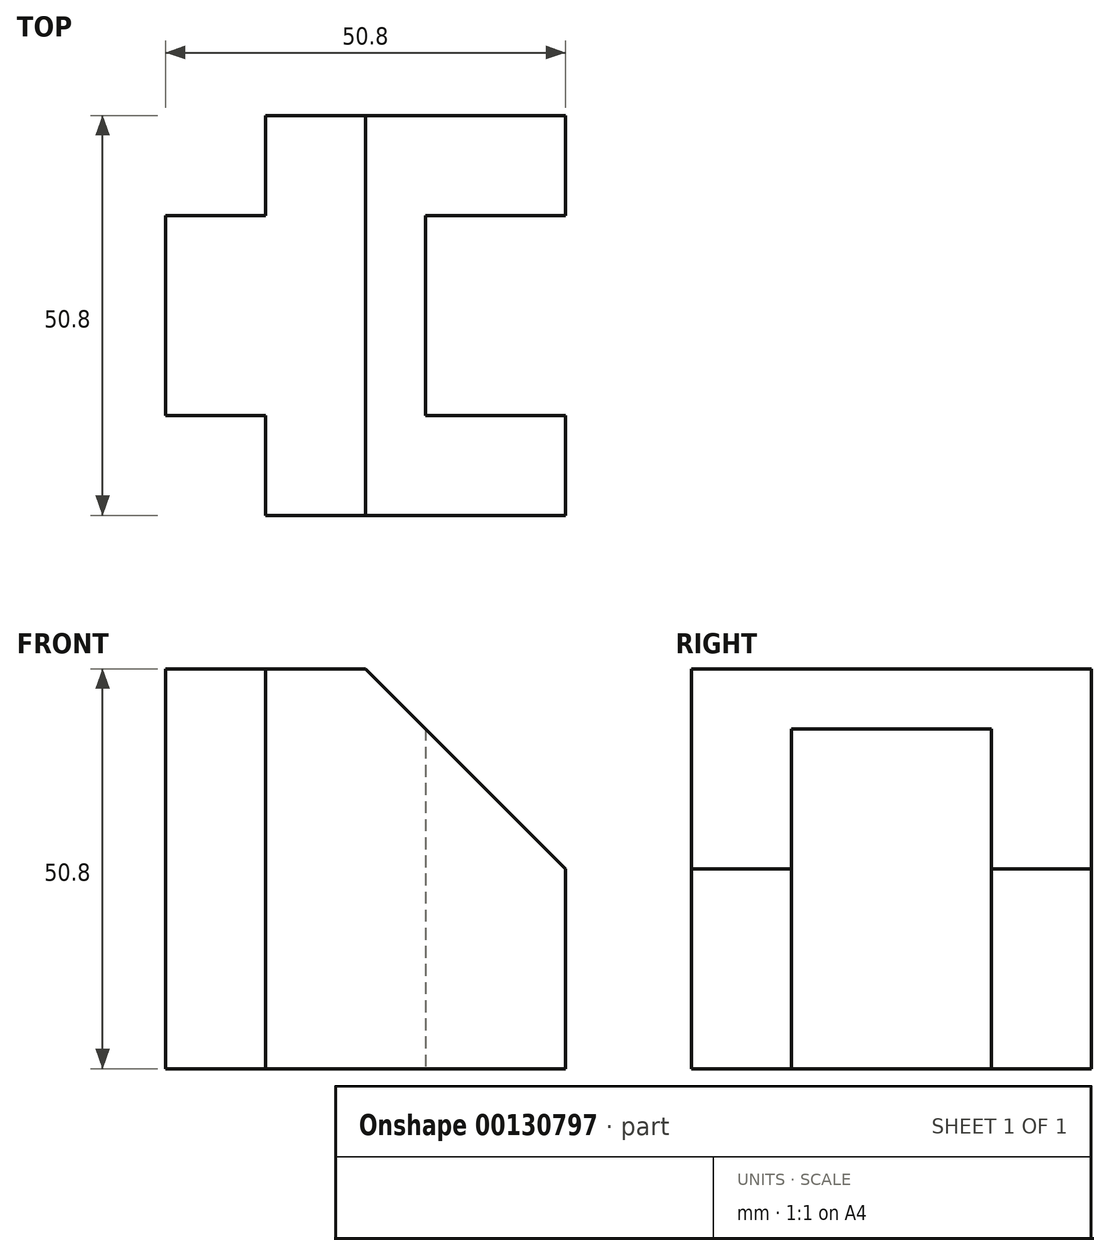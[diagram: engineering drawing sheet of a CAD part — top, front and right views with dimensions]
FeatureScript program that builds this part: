
annotation { "Feature Type Name" : "Feature", "Feature Type Description" : "" }
export const myFeature = defineFeature(function(context is Context, id is Id, definition is map)
    precondition{}
    {
        {
            var Q0;
            Q0=qCreatedBy(makeId("Top.planeOp"),FACE);
            var sketch = newSketch(context, id + "F0", { "sketchPlane" : qUnion([Q0])});
            skLineSegment(sketch, "E0", {"start": v(0, 0) * mm, "end": v(-12.7, 0) * mm});
            skLineSegment(sketch, "E1", {"start": v(-12.7, 0) * mm, "end": v(-12.7, -25.4) * mm});
            skLineSegment(sketch, "E2", {"start": v(-12.7, -25.4) * mm, "end": v(0, -25.4) * mm});
            skLineSegment(sketch, "E3", {"start": v(0, -25.4) * mm, "end": v(0, -38.1) * mm});
            skLineSegment(sketch, "E4", {"start": v(0, -38.1) * mm, "end": v(12.7, -38.1) * mm});
            skLineSegment(sketch, "E5", {"start": v(0, 0) * mm, "end": v(0, 12.7) * mm});
            skLineSegment(sketch, "E6", {"start": v(0, 12.7) * mm, "end": v(12.7, 12.7) * mm});
            skLineSegment(sketch, "E7", {"start": v(12.7, 12.7) * mm, "end": v(12.7, -38.1) * mm});
            skLineSegment(sketch, "E8", {"start": v(12.7, 12.7) * mm, "end": v(38.1, 12.7) * mm});
            skLineSegment(sketch, "E9", {"start": v(38.1, -38.1) * mm, "end": v(12.7, -38.1) * mm});
            skLineSegment(sketch, "E10", {"start": v(38.1, -38.1) * mm, "end": v(38.1, -25.4) * mm});
            skLineSegment(sketch, "E11", {"start": v(38.1, 12.7) * mm, "end": v(38.1, 0) * mm});
            skLineSegment(sketch, "E12", {"start": v(38.1, -25.4) * mm, "end": v(20.32, -25.4) * mm});
            skLineSegment(sketch, "E13", {"start": v(20.32, -25.4) * mm, "end": v(20.32, 0) * mm});
            skLineSegment(sketch, "E14", {"start": v(20.32, 0) * mm, "end": v(38.1, 0) * mm});
            skSolve(sketch);
        }
        {
            var Q0;
            Q0=makeQuery(id+"F0.imprint","IMPRINT",FACE,{"disambiguationData":[TD([[makeQuery(id+"F0.imprint","IMPRINT",EDGE,{"derivedFrom":sQuery(id+"F0.wireOp",EDGE,"E0")}),1.0]])]});
            var Q1;
            Q1=makeQuery(id+"F0.imprint","IMPRINT",FACE,{"disambiguationData":[TD([[makeQuery(id+"F0.imprint","IMPRINT",EDGE,{"derivedFrom":sQuery(id+"F0.wireOp",EDGE,"E7")}),1.0]])]});
            extrude(context, id + "F1", {"entities" : qUnion([Q0, Q1]), "depth" : 50.8 * mm});
        }
        {
            var Q0;
            Q0=makeQuery(id+"F1.opExtrude","SWEPT_FACE",FACE,{"disambiguationData":[OSD([sQuery(id+"F0.wireOp",EDGE,"E4"),sQuery(id+"F0.wireOp",EDGE,"E9")])]});
            var sketch = newSketch(context, id + "F2", { "sketchPlane" : qUnion([Q0])});
            skLineSegment(sketch, "E15.0", {"start": v(0, 50.8) * mm, "end": v(38.1, 50.8) * mm});
            skLineSegment(sketch, "E15.1", {"start": v(38.1, 50.8) * mm, "end": v(38.1, 0) * mm});
            skLineSegment(sketch, "E15.3", {"start": v(0, 0) * mm, "end": v(38.1, 0) * mm});
            skLineSegment(sketch, "E16", {"start": v(12.7, 50.8) * mm, "end": v(38.1, 25.4) * mm});
            skLineSegment(sketch, "E17", {"start": v(38.1, 25.4) * mm, "end": v(38.1, 50.8) * mm});
            skSolve(sketch);
        }
        {
            var Q0;
            {var subQ2=sQuery(id+"F2.wireOp",EDGE,"E16");Q0=makeQuery(id+"F2.imprint","IMPRINT",FACE,{"disambiguationData":[TD([[makeQuery(id+"F2.imprint","IMPRINT",EDGE,{"derivedFrom":subQ2}),1.0]])]});}
            extrude(context, id + "F3", {"entities" : qUnion([Q0]), "operationType" : NewBodyOperationType.REMOVE, "endBound" : BoundingType.THROUGH_ALL, "oppositeDirection" : true, "depth" : 25.4 * mm});
        }
    });
